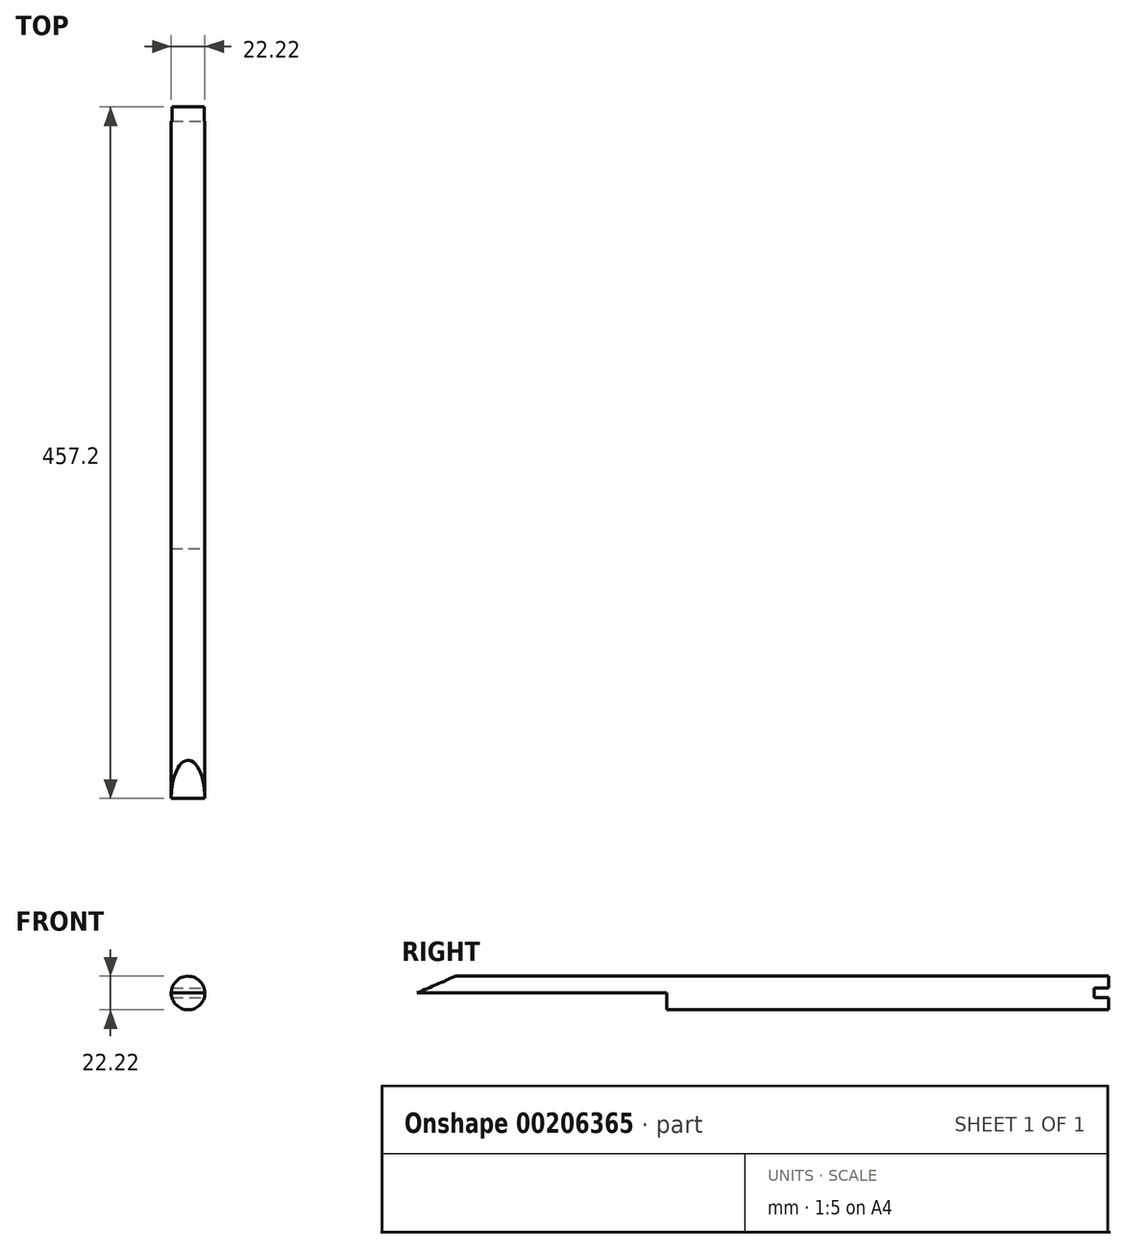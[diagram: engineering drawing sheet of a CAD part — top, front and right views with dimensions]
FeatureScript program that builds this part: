
annotation { "Feature Type Name" : "Feature", "Feature Type Description" : "" }
export const myFeature = defineFeature(function(context is Context, id is Id, definition is map)
    precondition{}
    {
        {
            var Q0;
            Q0=qCreatedBy(makeId("Front.planeOp"),FACE);
            var sketch = newSketch(context, id + "F0", { "sketchPlane" : qUnion([Q0])});
            skCircle(sketch, "E0", {"center": v(0, 0) * mm, "radius": 11.11 * mm});
            skSolve(sketch);
        }
        {
            var Q0;
            Q0 = qSketchRegion(id + "F0", true);
            extrude(context, id + "F1", {"entities" : qUnion([Q0]), "depth" : 457.2 * mm});
        }
        {
            var Q0;
            Q0=qCreatedBy(makeId("Right.planeOp"),FACE);
            var sketch = newSketch(context, id + "F2", { "sketchPlane" : qUnion([Q0])});
            skLineSegment(sketch, "E1.bottom", {"start": v(-457.2, 0) * mm, "end": v(-292.1, 0) * mm});
            skLineSegment(sketch, "E1.top", {"start": v(-457.2, -11.11) * mm, "end": v(-292.1, -11.11) * mm});
            skLineSegment(sketch, "E1.left", {"start": v(-457.2, 0) * mm, "end": v(-457.2, -11.11) * mm});
            skLineSegment(sketch, "E1.right", {"start": v(-292.1, 0) * mm, "end": v(-292.1, -11.11) * mm});
            skLineSegment(sketch, "E2.bottom", {"start": v(-9.52, 3.17) * mm, "end": v(9.53, 3.17) * mm});
            skLineSegment(sketch, "E2.top", {"start": v(-9.53, -3.18) * mm, "end": v(9.52, -3.18) * mm});
            skLineSegment(sketch, "E2.left", {"start": v(-9.52, 3.17) * mm, "end": v(-9.53, -3.18) * mm});
            skLineSegment(sketch, "E2.right", {"start": v(9.53, 3.17) * mm, "end": v(9.52, -3.18) * mm});
            skPoint(sketch, "E2.middle", {"position": v(0, 0) * mm});
            skLineSegment(sketch, "E3", {"start": v(-457.2, 0) * mm, "end": v(-431.8, 11.11) * mm});
            skLineSegment(sketch, "E4", {"start": v(-431.8, 11.11) * mm, "end": v(-457.2, 11.11) * mm});
            skLineSegment(sketch, "E5", {"start": v(-457.2, 11.11) * mm, "end": v(-457.2, 0) * mm});
            skSolve(sketch);
        }
        {
            var Q0;
            Q0 = qSketchRegion(id + "F2", true);
            extrude(context, id + "F3", {"entities" : qUnion([Q0]), "operationType" : NewBodyOperationType.REMOVE, "endBound" : BoundingType.SYMMETRIC, "oppositeDirection" : true, "depth" : 25.4 * mm});
        }
    });
